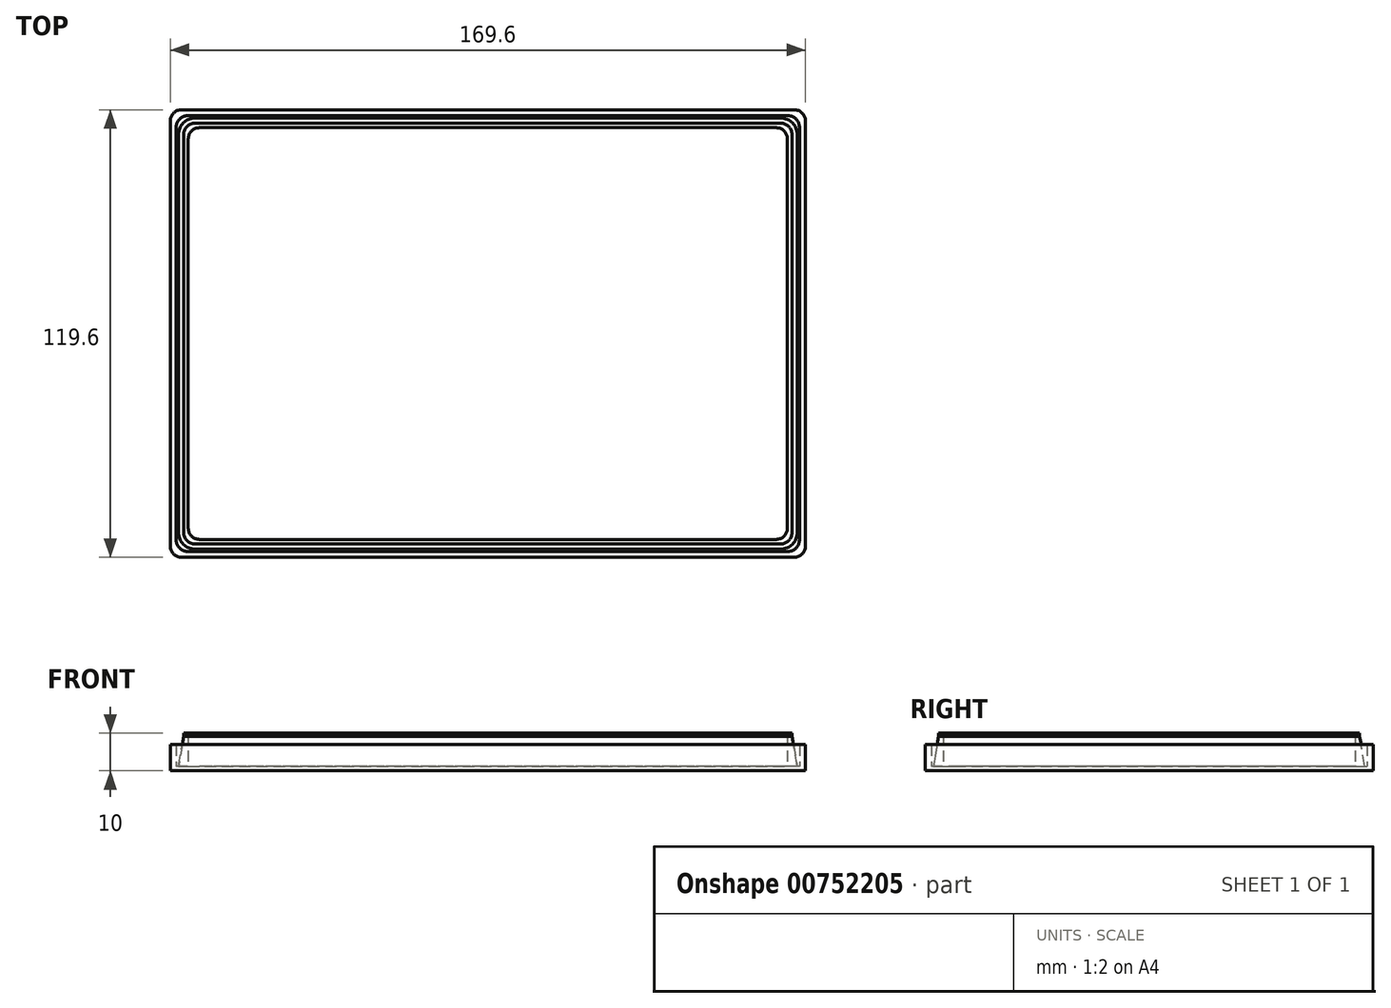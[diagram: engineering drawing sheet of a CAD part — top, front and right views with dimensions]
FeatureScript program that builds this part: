
annotation { "Feature Type Name" : "Feature", "Feature Type Description" : "" }
export const myFeature = defineFeature(function(context is Context, id is Id, definition is map)
    precondition{}
    {
        {
            var Q0;
            Q0=qCreatedBy(makeId("Top.planeOp"),FACE);
            var sketch = newSketch(context, id + "F0", { "sketchPlane" : qUnion([Q0])});
            skLineSegment(sketch, "E0.bottom", {"start": v(-77, 55) * mm, "end": v(77, 55) * mm});
            skLineSegment(sketch, "E0.top", {"start": v(-77, -55) * mm, "end": v(77, -55) * mm});
            skLineSegment(sketch, "E0.left", {"start": v(-80, 52) * mm, "end": v(-80, -52) * mm});
            skLineSegment(sketch, "E0.right", {"start": v(80, 52) * mm, "end": v(80, -52) * mm});
            skPoint(sketch, "E0.middle", {"position": v(0, 0) * mm});
            skLineSegment(sketch, "E1.bottom", {"start": v(-78.2, 56.2) * mm, "end": v(78.2, 56.2) * mm});
            skLineSegment(sketch, "E1.top", {"start": v(-78.2, -56.2) * mm, "end": v(78.2, -56.2) * mm});
            skLineSegment(sketch, "E1.left", {"start": v(-81.2, 53.2) * mm, "end": v(-81.2, -53.2) * mm});
            skLineSegment(sketch, "E1.right", {"start": v(81.2, 53.2) * mm, "end": v(81.2, -53.2) * mm});
            skLineSegment(sketch, "E2.bottom", {"start": v(80.2, -58.2) * mm, "end": v(-80.2, -58.2) * mm});
            skLineSegment(sketch, "E2.top", {"start": v(80.2, 58.2) * mm, "end": v(-80.2, 58.2) * mm});
            skLineSegment(sketch, "E2.left", {"start": v(83.2, -55.2) * mm, "end": v(83.2, 55.2) * mm});
            skLineSegment(sketch, "E2.right", {"start": v(-83.2, -55.2) * mm, "end": v(-83.2, 55.2) * mm});
            skLineSegment(sketch, "E3.bottom", {"start": v(-81.8, 59.8) * mm, "end": v(81.8, 59.8) * mm});
            skLineSegment(sketch, "E3.top", {"start": v(-81.8, -59.8) * mm, "end": v(81.8, -59.8) * mm});
            skLineSegment(sketch, "E3.left", {"start": v(-84.8, 56.8) * mm, "end": v(-84.8, -56.8) * mm});
            skLineSegment(sketch, "E3.right", {"start": v(84.8, 56.8) * mm, "end": v(84.8, -56.8) * mm});
            skPoint(sketch, "E4.visualSharp", {"position": v(-84.8, 59.8) * mm});
            skArc(sketch, "E4.filletArc", {"start": v(-81.8, 59.8) * mm, "mid": v(-83.92, 58.92) * mm, "end": v(-84.8, 56.8) * mm});
            skPoint(sketch, "E5.visualSharp", {"position": v(-83.2, 58.2) * mm});
            skArc(sketch, "E5.filletArc", {"start": v(-80.2, 58.2) * mm, "mid": v(-82.32, 57.32) * mm, "end": v(-83.2, 55.2) * mm});
            skPoint(sketch, "E6.visualSharp", {"position": v(-81.2, 56.2) * mm});
            skArc(sketch, "E6.filletArc", {"start": v(-78.2, 56.2) * mm, "mid": v(-80.32, 55.32) * mm, "end": v(-81.2, 53.2) * mm});
            skPoint(sketch, "E7.visualSharp", {"position": v(-80, 55) * mm});
            skArc(sketch, "E7.filletArc", {"start": v(-77, 55) * mm, "mid": v(-79.12, 54.12) * mm, "end": v(-80, 52) * mm});
            skPoint(sketch, "E8.visualSharp", {"position": v(80, 55) * mm});
            skArc(sketch, "E8.filletArc", {"start": v(80, 52) * mm, "mid": v(79.12, 54.12) * mm, "end": v(77, 55) * mm});
            skPoint(sketch, "E9.visualSharp", {"position": v(81.2, 56.2) * mm});
            skArc(sketch, "E9.filletArc", {"start": v(81.2, 53.2) * mm, "mid": v(80.32, 55.32) * mm, "end": v(78.2, 56.2) * mm});
            skPoint(sketch, "E10.visualSharp", {"position": v(83.2, 58.2) * mm});
            skArc(sketch, "E10.filletArc", {"start": v(83.2, 55.2) * mm, "mid": v(82.32, 57.32) * mm, "end": v(80.2, 58.2) * mm});
            skPoint(sketch, "E11.visualSharp", {"position": v(84.8, 59.8) * mm});
            skArc(sketch, "E11.filletArc", {"start": v(84.8, 56.8) * mm, "mid": v(83.92, 58.92) * mm, "end": v(81.8, 59.8) * mm});
            skPoint(sketch, "E12.visualSharp", {"position": v(80, -55) * mm});
            skArc(sketch, "E12.filletArc", {"start": v(77, -55) * mm, "mid": v(79.12, -54.12) * mm, "end": v(80, -52) * mm});
            skPoint(sketch, "E13.visualSharp", {"position": v(81.2, -56.2) * mm});
            skArc(sketch, "E13.filletArc", {"start": v(78.2, -56.2) * mm, "mid": v(80.32, -55.32) * mm, "end": v(81.2, -53.2) * mm});
            skPoint(sketch, "E14.visualSharp", {"position": v(83.2, -58.2) * mm});
            skArc(sketch, "E14.filletArc", {"start": v(80.2, -58.2) * mm, "mid": v(82.32, -57.32) * mm, "end": v(83.2, -55.2) * mm});
            skPoint(sketch, "E15.visualSharp", {"position": v(84.8, -59.8) * mm});
            skArc(sketch, "E15.filletArc", {"start": v(81.8, -59.8) * mm, "mid": v(83.92, -58.92) * mm, "end": v(84.8, -56.8) * mm});
            skPoint(sketch, "E16.visualSharp", {"position": v(-80, -55) * mm});
            skArc(sketch, "E16.filletArc", {"start": v(-80, -52) * mm, "mid": v(-79.12, -54.12) * mm, "end": v(-77, -55) * mm});
            skPoint(sketch, "E17.visualSharp", {"position": v(-81.2, -56.2) * mm});
            skArc(sketch, "E17.filletArc", {"start": v(-81.2, -53.2) * mm, "mid": v(-80.32, -55.32) * mm, "end": v(-78.2, -56.2) * mm});
            skPoint(sketch, "E18.visualSharp", {"position": v(-83.2, -58.2) * mm});
            skArc(sketch, "E18.filletArc", {"start": v(-83.2, -55.2) * mm, "mid": v(-82.32, -57.32) * mm, "end": v(-80.2, -58.2) * mm});
            skPoint(sketch, "E19.visualSharp", {"position": v(-84.8, -59.8) * mm});
            skArc(sketch, "E19.filletArc", {"start": v(-84.8, -56.8) * mm, "mid": v(-83.92, -58.92) * mm, "end": v(-81.8, -59.8) * mm});
            skSolve(sketch);
        }
        {
            var Q0;
            Q0=makeQuery(id+"F0.imprint","IMPRINT",FACE,{"disambiguationData":[TD([[makeQuery(id+"F0.imprint","IMPRINT",EDGE,{"derivedFrom":sQuery(id+"F0.wireOp",EDGE,"E0.bottom")}),-1.0]])]});
            var Q1;
            Q1=makeQuery(id+"F0.imprint","IMPRINT",FACE,{"disambiguationData":[TD([[makeQuery(id+"F0.imprint","IMPRINT",EDGE,{"derivedFrom":sQuery(id+"F0.wireOp",EDGE,"E0.bottom")}),1.0]])]});
            var Q2;
            Q2=makeQuery(id+"F0.imprint","IMPRINT",FACE,{"disambiguationData":[TD([[makeQuery(id+"F0.imprint","IMPRINT",EDGE,{"derivedFrom":sQuery(id+"F0.wireOp",EDGE,"E1.bottom")}),1.0]])]});
            var Q3;
            Q3=makeQuery(id+"F0.imprint","IMPRINT",FACE,{"disambiguationData":[TD([[makeQuery(id+"F0.imprint","IMPRINT",EDGE,{"derivedFrom":sQuery(id+"F0.wireOp",EDGE,"E2.bottom")}),1.0]])]});
            extrude(context, id + "F1", {"entities" : qUnion([Q0, Q1, Q2, Q3]), "depth" : 1.2 * mm, "offsetDistance" : 25 * mm});
        }
        {
            var Q0;
            Q0=makeQuery(id+"F0.imprint","IMPRINT",FACE,{"disambiguationData":[TD([[makeQuery(id+"F0.imprint","IMPRINT",EDGE,{"derivedFrom":sQuery(id+"F0.wireOp",EDGE,"E0.bottom")}),1.0]])]});
            extrude(context, id + "F2", {"entities" : qUnion([Q0]), "operationType" : NewBodyOperationType.ADD, "depth" : 10 * mm, "offsetDistance" : 25 * mm});
        }
        {
            var Q0;
            Q0=makeQuery(id+"F0.imprint","IMPRINT",FACE,{"disambiguationData":[TD([[makeQuery(id+"F0.imprint","IMPRINT",EDGE,{"derivedFrom":sQuery(id+"F0.wireOp",EDGE,"E2.bottom")}),1.0]])]});
            extrude(context, id + "F3", {"entities" : qUnion([Q0]), "operationType" : NewBodyOperationType.ADD, "depth" : 7 * mm, "offsetDistance" : 25 * mm});
        }
        {
            var Q0;
            Q0=makeQuery(id+"F2.boolean.opBoolean","INTERSECT",EDGE,{"derivedFrom":[makeQuery(id+"F1.opExtrude","CAP_FACE",FACE,{"disambiguationData":[OSD([sQuery(id+"F0.wireOp",EDGE,"E3.bottom"),sQuery(id+"F0.wireOp",EDGE,"E3.top"),sQuery(id+"F0.wireOp",EDGE,"E3.left"),sQuery(id+"F0.wireOp",EDGE,"E3.right"),sQuery(id+"F0.wireOp",EDGE,"E4.filletArc"),sQuery(id+"F0.wireOp",EDGE,"E11.filletArc"),sQuery(id+"F0.wireOp",EDGE,"E15.filletArc"),sQuery(id+"F0.wireOp",EDGE,"E19.filletArc")])],"isStart":false}),makeQuery(id+"F2.opExtrude","SWEPT_FACE",FACE,{"disambiguationData":[OSD([sQuery(id+"F0.wireOp",EDGE,"E1.left")])]})]});
            chamfer(context, id + "F4", {"entities" : qUnion([Q0]), "chamferType" : ChamferType.TWO_OFFSETS, "width1" : 1.4 * mm, "oppositeDirection" : false, "width2" : 8 * mm, "tangentPropagation" : true});
        }
    });
